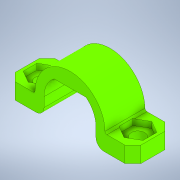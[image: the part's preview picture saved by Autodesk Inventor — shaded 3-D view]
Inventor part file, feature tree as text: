
AUTODESK INVENTOR PART (.ipt)
format: ipt  version: 2020 (Build 240168000, 168)  size: 187,904 bytes
history: native  units: mm
features: extrude x4, sketch x2, chamfer x1
ambient origin geometry x8: Origin, YZ Plane, XZ Plane, XY Plane, X Axis, Y Axis, Z Axis, Center Point
bodies: Solid1 (feature_tree)
feature tree (7):
  extrude  "Extrusion1"  Depth=2.0mm
  chamfer  "Chamfer1"  Distance=0.5mm
  sketch  "Sketch2"  dims[d6=6.5mm d7=0.5mm d9=0.5mm d10=4.0mm d11=6.5mm d12=6.5mm d13=10.0mm d14=25.0mm d15=10.0mm d16=0.0mm d17=2.0mm d18=2.0mm d19=45.0deg d20=24.0mm d21=3.4mm d22=6.0mm d23=10.0mm d24=0.0mm d25=0.0mm d26=0.0mm d27=1.5mm d28=0.0mm]
  extrude  "Extrusion2"  Depth=0.5mm
  extrude  "Extrusion3"  Depth=4.0mm
  extrude  "Extrusion4"  Depth=6.5mm
  sketch  "Sketch1"  dims[d0=4.0mm d4=2.0mm]
